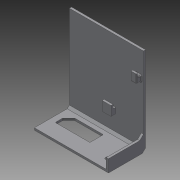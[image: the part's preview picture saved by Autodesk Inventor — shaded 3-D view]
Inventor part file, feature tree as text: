
AUTODESK INVENTOR PART (.ipt)
format: ipt  version: 2015 SP1 (Build 190203100, 203)  size: 194,560 bytes
history: native  units: mm
features: extrude x5, sketch x5, chamfer x4, fillet x2, plane x2
ambient origin geometry x8: Origin, YZ Plane, XZ Plane, XY Plane, X Axis, Y Axis, Z Axis, Center Point
bodies: Solid1 (feature_tree)
feature tree (18):
  extrude  "Extrusion1"  Depth=47.0mm
  extrude  "Extrusion2"  Depth=18.65mm TaperAngle=0.0deg
  chamfer  "Chamfer1"  Distance=1.15mm Angle=45.0deg
  chamfer  "Chamfer3"  Distance=2.0mm Angle=45.0deg
  extrude  "Extrusion3"  TaperAngle=135.0deg  [1 undecoded]
  chamfer  "Chamfer4"  Angle=135.0deg  [1 undecoded]
  chamfer  "Chamfer5"  Distance=18.5mm
  fillet  "Fillet1"  Radius=7.2mm
  plane  "Work Plane1"
  extrude  "Extrusion4"  Depth=2.5mm
  plane  "Work Plane2"
  extrude  "Extrusion5"  Depth=2.5mm
  fillet  "Fillet4"  Radius=8.0mm
  sketch  "Sketch1"  dims[d0=39.5mm d1=47.0mm]
  sketch  "Sketch2"  dims[d2=1.15mm d3=0.0mm d4=18.65mm d5=0.0mm]
  sketch  "Sketch3"  dims[d7=6.6mm]
  sketch  "Sketch5"  dims[d9=1.15mm d10=1.15mm d11=2.0mm d12=45.0deg d16=1.75mm d17=2.0mm d18=45.0deg]
  sketch  "Sketch6"  dims[d19=2.7mm d21=135.0deg d22=135.0deg d24=18.5mm d25=7.2mm d34=5.5mm d35=5.5mm d36=8.0mm d38=1.15mm d39=0.0mm d40=2.0mm d41=2.0mm d42=45.0deg d43=3.1mm d44=1.5mm d45=0.75mm d46=45.0deg d47=4.0mm d48=0.5mm d49=-1.25mm d50=3.0mm d51=0.0mm d52=4.8mm d55=1.5mm d57=31.0mm d58=3.0mm d60=0.5mm d61=-14.8mm d62=5.0mm d63=2.0mm d64=2.5mm d66=4.75mm d67=0.0mm d68=9.5mm d69=1.4mm d70=2.5mm]
note: 2 required parameter values undecoded (feature->parameter linkage not recoverable at this tier; creation-order binding heuristic only, values carry confidence <= 0.55)
